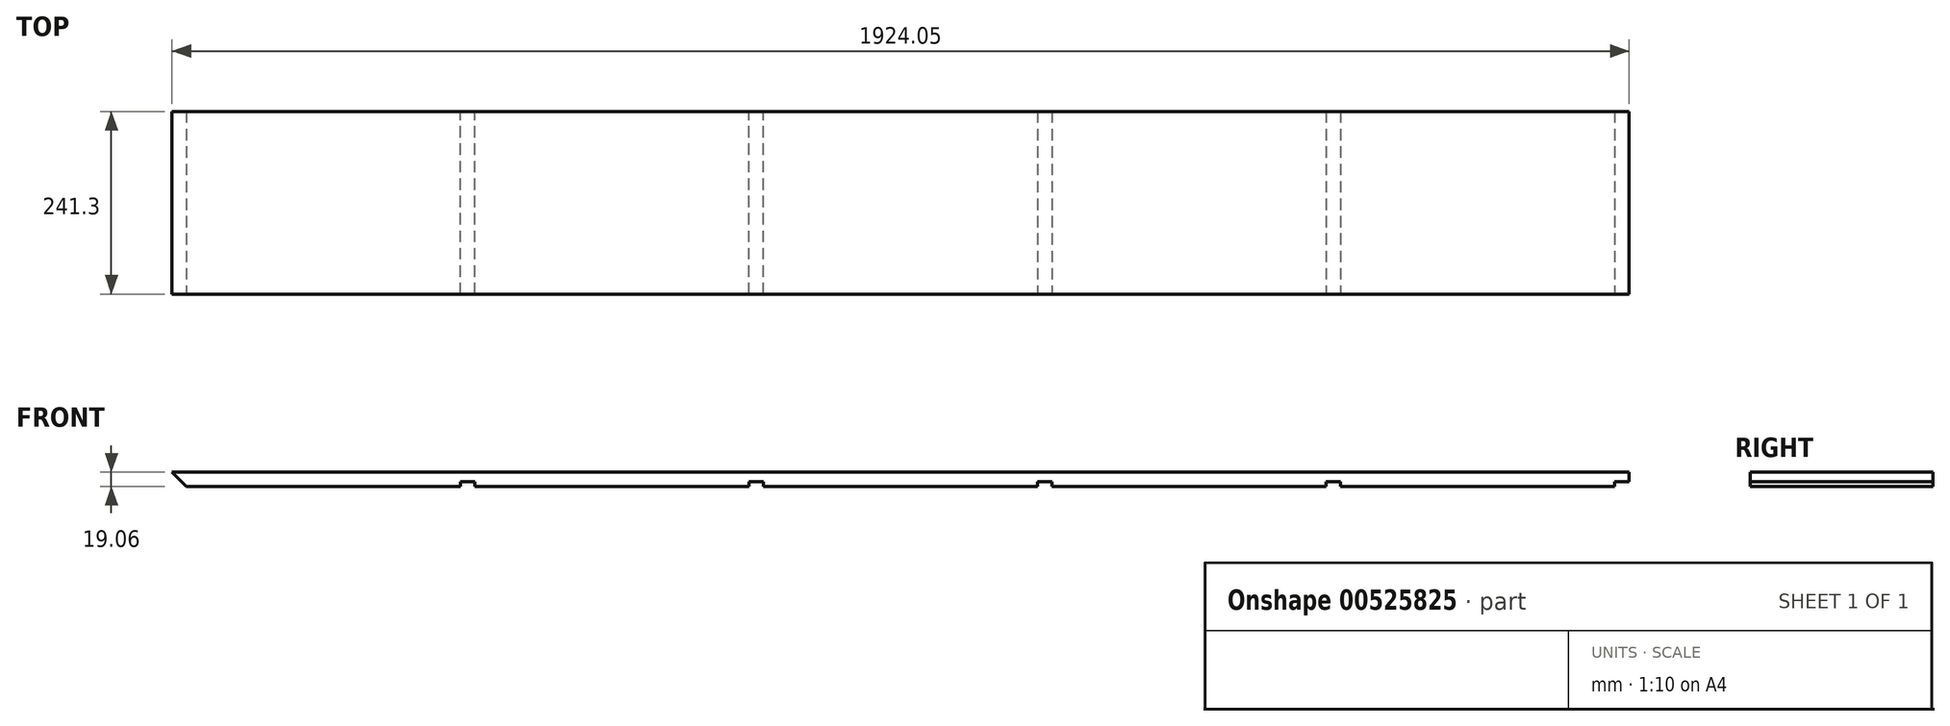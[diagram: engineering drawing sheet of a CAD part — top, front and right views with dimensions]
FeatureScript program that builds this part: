
annotation { "Feature Type Name" : "Feature", "Feature Type Description" : "" }
export const myFeature = defineFeature(function(context is Context, id is Id, definition is map)
    precondition{}
    {
        {
            var Q0;
            Q0=qCreatedBy(makeId("Front.planeOp"),FACE);
            var sketch = newSketch(context, id + "F0", { "sketchPlane" : qUnion([Q0])});
            skLineSegment(sketch, "E0.bottom", {"start": v(962.03, -9.53) * mm, "end": v(-962.03, -9.53) * mm});
            skLineSegment(sketch, "E0.top", {"start": v(962.03, 9.53) * mm, "end": v(-962.03, 9.53) * mm});
            skLineSegment(sketch, "E0.left", {"start": v(962.03, -9.53) * mm, "end": v(962.03, 9.52) * mm});
            skLineSegment(sketch, "E0.right", {"start": v(-962.03, -9.53) * mm, "end": v(-962.03, 9.52) * mm});
            skPoint(sketch, "E0.middle", {"position": v(0, 0) * mm});
            skSolve(sketch);
        }
        {
            var Q0;
            Q0=qSketchRegion(id+"F0",true);
            extrude(context, id + "F1", {"entities" : qUnion([Q0]), "depth" : 241.3 * mm});
        }
        {
            var Q0;
            Q0=makeQuery(id+"F1.opExtrude","CAP_FACE",FACE,{"disambiguationData":[OSD([sQuery(id+"F0.wireOp",EDGE,"E0.bottom"),sQuery(id+"F0.wireOp",EDGE,"E0.top"),sQuery(id+"F0.wireOp",EDGE,"E0.left"),sQuery(id+"F0.wireOp",EDGE,"E0.right")])],"isStart":false});
            var sketch = newSketch(context, id + "F2", { "sketchPlane" : qUnion([Q0])});
            skLineSegment(sketch, "E1", {"start": v(-962.03, 9.52) * mm, "end": v(-962.03, -9.53) * mm});
            skLineSegment(sketch, "E2", {"start": v(-962.03, -9.53) * mm, "end": v(-942.98, -9.53) * mm});
            skLineSegment(sketch, "E3", {"start": v(-942.98, -9.53) * mm, "end": v(-962.03, 9.52) * mm});
            skSolve(sketch);
        }
        {
            var Q0;
            Q0=qSketchRegion(id+"F2",true);
            extrude(context, id + "F3", {"entities" : qUnion([Q0]), "operationType" : NewBodyOperationType.REMOVE, "endBound" : BoundingType.THROUGH_ALL, "oppositeDirection" : true, "depth" : 25.4 * mm});
        }
        {
            var Q0;
            Q0=makeQuery(id+"F1.opExtrude","CAP_FACE",FACE,{"disambiguationData":[OSD([sQuery(id+"F0.wireOp",EDGE,"E0.bottom"),sQuery(id+"F0.wireOp",EDGE,"E0.top"),sQuery(id+"F0.wireOp",EDGE,"E0.left"),sQuery(id+"F0.wireOp",EDGE,"E0.right")])],"isStart":false});
            var sketch = newSketch(context, id + "F4", { "sketchPlane" : qUnion([Q0])});
            skPoint(sketch, "E4.endSnap0", {"position": v(0, 9.53) * mm});
            skLineSegment(sketch, "E5", {"start": v(-571.5, 29.3) * mm, "end": v(-571.5, -29.74) * mm, "construction": true});
            skLineSegment(sketch, "E6", {"start": v(571.5, 31.76) * mm, "end": v(571.5, -37.12) * mm, "construction": true});
            skLineSegment(sketch, "E7", {"start": v(190.5, 28.1) * mm, "end": v(190.5, -36.6) * mm, "construction": true});
            skLineSegment(sketch, "E8", {"start": v(-190.5, 33.67) * mm, "end": v(-190.5, -36.6) * mm, "construction": true});
            skLineSegment(sketch, "E9.bottom", {"start": v(-561.98, -3.18) * mm, "end": v(-581.02, -3.18) * mm});
            skLineSegment(sketch, "E9.top", {"start": v(-561.98, -15.88) * mm, "end": v(-581.02, -15.88) * mm});
            skLineSegment(sketch, "E9.left", {"start": v(-561.98, -3.18) * mm, "end": v(-561.98, -15.88) * mm});
            skLineSegment(sketch, "E9.right", {"start": v(-581.02, -3.18) * mm, "end": v(-581.02, -15.88) * mm});
            skPoint(sketch, "E9.middle", {"position": v(-571.5, -9.53) * mm});
            skLineSegment(sketch, "E10.bottom", {"start": v(-180.97, -3.18) * mm, "end": v(-200.02, -3.18) * mm});
            skLineSegment(sketch, "E10.top", {"start": v(-180.97, -15.88) * mm, "end": v(-200.02, -15.88) * mm});
            skLineSegment(sketch, "E10.left", {"start": v(-180.97, -3.18) * mm, "end": v(-180.97, -15.88) * mm});
            skLineSegment(sketch, "E10.right", {"start": v(-200.02, -3.18) * mm, "end": v(-200.02, -15.88) * mm});
            skPoint(sketch, "E10.middle", {"position": v(-190.5, -9.53) * mm});
            skPoint(sketch, "E11.middle", {"position": v(190.5, -9.53) * mm});
            skPoint(sketch, "E12.middle", {"position": v(571.5, -9.53) * mm});
            skLineSegment(sketch, "E13.bottom", {"start": v(581.03, -15.88) * mm, "end": v(561.98, -15.88) * mm});
            skLineSegment(sketch, "E13.top", {"start": v(581.03, -3.18) * mm, "end": v(561.98, -3.18) * mm});
            skLineSegment(sketch, "E13.left", {"start": v(581.03, -15.88) * mm, "end": v(581.03, -3.18) * mm});
            skLineSegment(sketch, "E13.right", {"start": v(561.98, -15.88) * mm, "end": v(561.98, -3.18) * mm});
            skLineSegment(sketch, "E14.bottom", {"start": v(200.03, -15.88) * mm, "end": v(180.98, -15.88) * mm});
            skLineSegment(sketch, "E14.top", {"start": v(200.03, -3.18) * mm, "end": v(180.98, -3.18) * mm});
            skLineSegment(sketch, "E14.left", {"start": v(200.03, -15.88) * mm, "end": v(200.03, -3.18) * mm});
            skLineSegment(sketch, "E14.right", {"start": v(180.98, -15.88) * mm, "end": v(180.98, -3.18) * mm});
            skLineSegment(sketch, "E15.bottom", {"start": v(942.98, -9.53) * mm, "end": v(962.03, -9.53) * mm});
            skLineSegment(sketch, "E15.top", {"start": v(942.98, -3.18) * mm, "end": v(962.03, -3.18) * mm});
            skLineSegment(sketch, "E15.left", {"start": v(942.98, -9.53) * mm, "end": v(942.98, -3.18) * mm});
            skLineSegment(sketch, "E15.right", {"start": v(962.03, -9.53) * mm, "end": v(962.03, -3.18) * mm});
            skSolve(sketch);
        }
        {
            var Q0;
            Q0=qSketchRegion(id+"F4",true);
            extrude(context, id + "F5", {"entities" : qUnion([Q0]), "operationType" : NewBodyOperationType.REMOVE, "endBound" : BoundingType.THROUGH_ALL, "oppositeDirection" : true, "depth" : 25.4 * mm});
        }
    });
